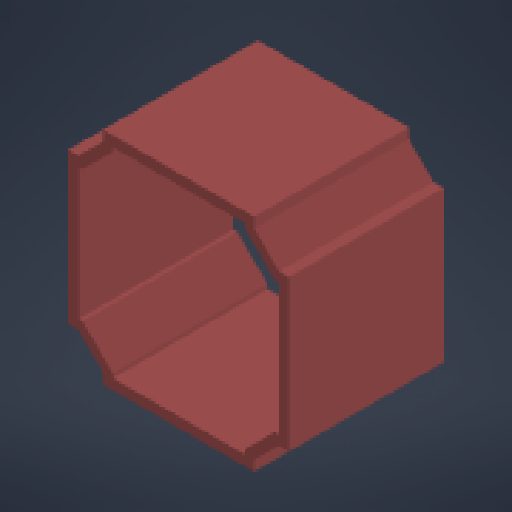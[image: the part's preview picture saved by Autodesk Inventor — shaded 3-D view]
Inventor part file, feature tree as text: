
AUTODESK INVENTOR PART (.ipt)
format: ipt  version: 2023.4 (Build 274418000, 418)  size: 158,720 bytes
history: native  units: mm
features: other x2, plane x1, extrude x1, reference x1
ambient origin geometry x8: Origin, YZ Plane, XZ Plane, XY Plane, X Axis, Y Axis, Z Axis, Center Point
bodies: Solid1 (feature_tree)
feature tree (5):
  plane  "Work Plane1"
  extrude  "Extrusion1"  Depth=0.075mm
  reference  "Reference1"
  other  "Cube 1x1 V5.iam"
  other  "Cube 1x1 Bottom V5:1"
